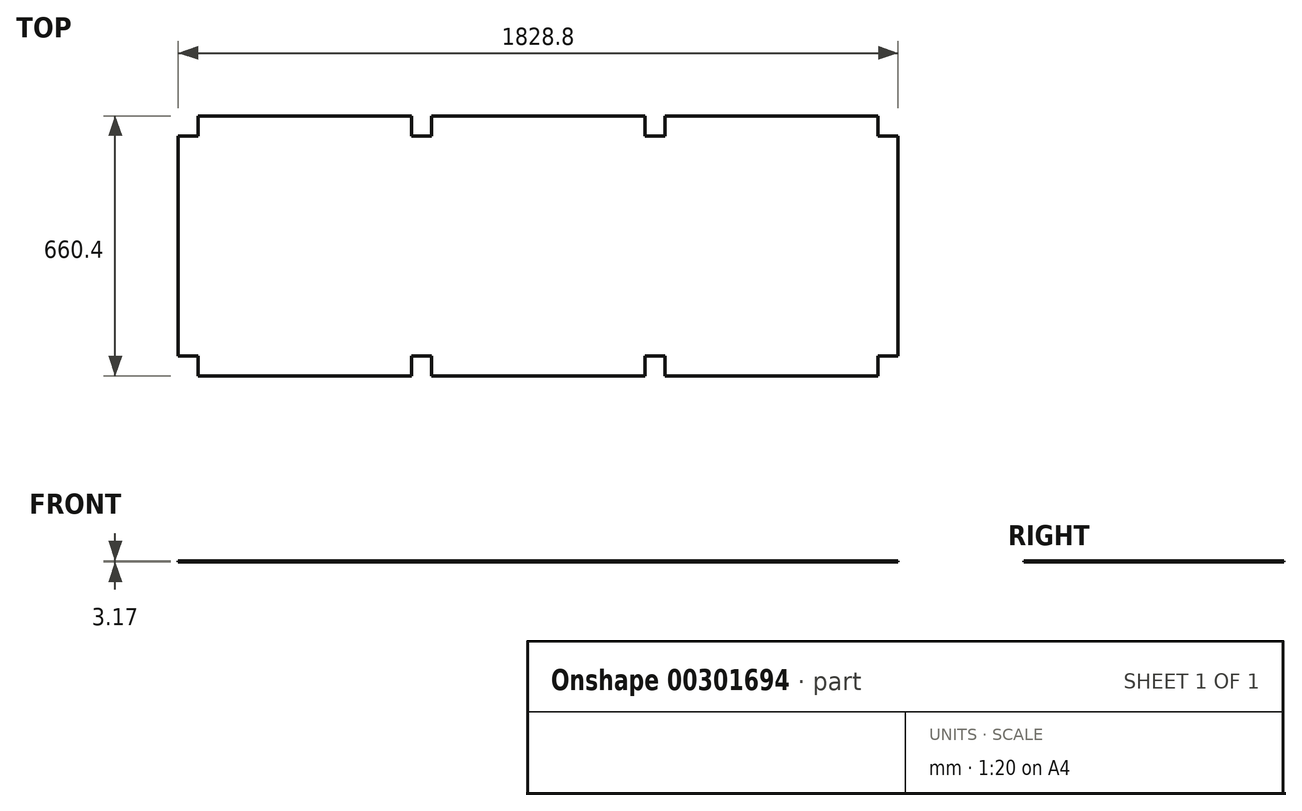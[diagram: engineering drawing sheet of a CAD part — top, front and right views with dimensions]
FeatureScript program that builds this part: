
annotation { "Feature Type Name" : "Feature", "Feature Type Description" : "" }
export const myFeature = defineFeature(function(context is Context, id is Id, definition is map)
    precondition{}
    {
        {
            var Q0;
            Q0=qCreatedBy(makeId("Top.planeOp"),FACE);
            var sketch = newSketch(context, id + "F0", { "sketchPlane" : qUnion([Q0])});
            skLineSegment(sketch, "E0.bottom", {"start": v(-863.6, -279.4) * mm, "end": v(863.6, -279.4) * mm});
            skLineSegment(sketch, "E0.top", {"start": v(-863.6, 279.4) * mm, "end": v(863.6, 279.4) * mm});
            skLineSegment(sketch, "E0.left", {"start": v(-863.6, -279.4) * mm, "end": v(-863.6, 279.4) * mm});
            skLineSegment(sketch, "E0.right", {"start": v(863.6, -279.4) * mm, "end": v(863.6, 279.4) * mm});
            skPoint(sketch, "E0.middle", {"position": v(0, 0) * mm});
            skLineSegment(sketch, "E1.bottom", {"start": v(-863.6, -279.4) * mm, "end": v(-914.4, -279.4) * mm});
            skLineSegment(sketch, "E1.top", {"start": v(-863.6, 279.4) * mm, "end": v(-914.4, 279.4) * mm});
            skLineSegment(sketch, "E1.right", {"start": v(-914.4, -279.4) * mm, "end": v(-914.4, 279.4) * mm});
            skPoint(sketch, "E1.middle", {"position": v(-889, 0) * mm});
            skLineSegment(sketch, "E2.bottom", {"start": v(863.6, -279.4) * mm, "end": v(914.4, -279.4) * mm});
            skLineSegment(sketch, "E2.top", {"start": v(863.6, 279.4) * mm, "end": v(914.4, 279.4) * mm});
            skLineSegment(sketch, "E2.right", {"start": v(914.4, -279.4) * mm, "end": v(914.4, 279.4) * mm});
            skPoint(sketch, "E2.middle", {"position": v(889, 0) * mm});
            skPoint(sketch, "E2.middle.positionSnap0", {"position": v(863.6, 0) * mm});
            skPoint(sketch, "E2.centerSnap0", {"position": v(863.6, 0) * mm});
            skLineSegment(sketch, "E3.bottom", {"start": v(270.9, 279.4) * mm, "end": v(-270.9, 279.4) * mm});
            skLineSegment(sketch, "E3.top", {"start": v(270.9, 330.2) * mm, "end": v(-270.9, 330.2) * mm});
            skLineSegment(sketch, "E3.left", {"start": v(270.9, 279.4) * mm, "end": v(270.9, 330.2) * mm});
            skLineSegment(sketch, "E3.right", {"start": v(-270.9, 279.4) * mm, "end": v(-270.9, 330.2) * mm});
            skPoint(sketch, "E3.middle", {"position": v(0, 304.8) * mm});
            skPoint(sketch, "E3.middle.positionSnap0", {"position": v(0, 279.4) * mm});
            skPoint(sketch, "E3.centerSnap0", {"position": v(0, 279.4) * mm});
            skLineSegment(sketch, "E4.bottom", {"start": v(270.9, -279.4) * mm, "end": v(-270.9, -279.4) * mm});
            skLineSegment(sketch, "E4.top", {"start": v(270.9, -330.2) * mm, "end": v(-270.9, -330.2) * mm});
            skLineSegment(sketch, "E4.left", {"start": v(270.9, -279.4) * mm, "end": v(270.9, -330.2) * mm});
            skLineSegment(sketch, "E4.right", {"start": v(-270.9, -279.4) * mm, "end": v(-270.9, -330.2) * mm});
            skPoint(sketch, "E4.middle", {"position": v(0, -304.8) * mm});
            skPoint(sketch, "E4.middle.positionSnap0", {"position": v(0, -279.4) * mm});
            skPoint(sketch, "E4.centerSnap0", {"position": v(0, -279.4) * mm});
            skLineSegment(sketch, "E5.bottom", {"start": v(863.68, -279.3) * mm, "end": v(321.9, -279.3) * mm});
            skLineSegment(sketch, "E5.top", {"start": v(863.68, -330.1) * mm, "end": v(321.9, -330.1) * mm});
            skLineSegment(sketch, "E5.left", {"start": v(863.68, -279.3) * mm, "end": v(863.68, -330.1) * mm});
            skLineSegment(sketch, "E5.right", {"start": v(321.9, -279.3) * mm, "end": v(321.9, -330.1) * mm});
            skPoint(sketch, "E5.middle", {"position": v(592.79, -304.7) * mm});
            skPoint(sketch, "E5.middle.positionSnap0", {"position": v(592.79, -262.28) * mm});
            skPoint(sketch, "E5.centerSnap0", {"position": v(592.79, -262.28) * mm});
            skLineSegment(sketch, "E6.bottom", {"start": v(-321.83, -279.38) * mm, "end": v(-863.6, -279.38) * mm});
            skLineSegment(sketch, "E6.top", {"start": v(-321.83, -330.18) * mm, "end": v(-863.6, -330.18) * mm});
            skLineSegment(sketch, "E6.left", {"start": v(-321.83, -279.38) * mm, "end": v(-321.83, -330.18) * mm});
            skLineSegment(sketch, "E6.right", {"start": v(-863.6, -279.38) * mm, "end": v(-863.6, -330.18) * mm});
            skPoint(sketch, "E6.middle", {"position": v(-592.72, -304.78) * mm});
            skPoint(sketch, "E6.middle.positionSnap0", {"position": v(-592.72, -282.03) * mm});
            skPoint(sketch, "E6.centerSnap0", {"position": v(-592.72, -282.03) * mm});
            skLineSegment(sketch, "E7.bottom", {"start": v(-321.62, 330.02) * mm, "end": v(-863.4, 330.02) * mm});
            skLineSegment(sketch, "E7.top", {"start": v(-321.62, 279.22) * mm, "end": v(-863.4, 279.22) * mm});
            skLineSegment(sketch, "E7.left", {"start": v(-321.62, 330.02) * mm, "end": v(-321.62, 279.22) * mm});
            skLineSegment(sketch, "E7.right", {"start": v(-863.4, 330.02) * mm, "end": v(-863.4, 279.22) * mm});
            skPoint(sketch, "E7.middle", {"position": v(-592.51, 304.62) * mm});
            skPoint(sketch, "E7.middle.positionSnap0", {"position": v(-592.51, 321.53) * mm});
            skPoint(sketch, "E7.centerSnap0", {"position": v(-592.51, 321.53) * mm});
            skLineSegment(sketch, "E8.bottom", {"start": v(863.59, 330.12) * mm, "end": v(321.8, 330.12) * mm});
            skLineSegment(sketch, "E8.top", {"start": v(863.59, 279.32) * mm, "end": v(321.8, 279.32) * mm});
            skLineSegment(sketch, "E8.left", {"start": v(863.59, 330.12) * mm, "end": v(863.59, 279.32) * mm});
            skLineSegment(sketch, "E8.right", {"start": v(321.8, 330.12) * mm, "end": v(321.8, 279.32) * mm});
            skPoint(sketch, "E8.middle", {"position": v(592.7, 304.72) * mm});
            skPoint(sketch, "E8.middle.positionSnap0", {"position": v(592.7, 327.12) * mm});
            skPoint(sketch, "E8.centerSnap0", {"position": v(592.7, 327.12) * mm});
            skSolve(sketch);
        }
        {
            var Q0;
            Q0 = qSketchRegion(id + "F0", true);
            extrude(context, id + "F1", {"entities" : qUnion([Q0]), "depth" : 3.17 * mm});
        }
    });
